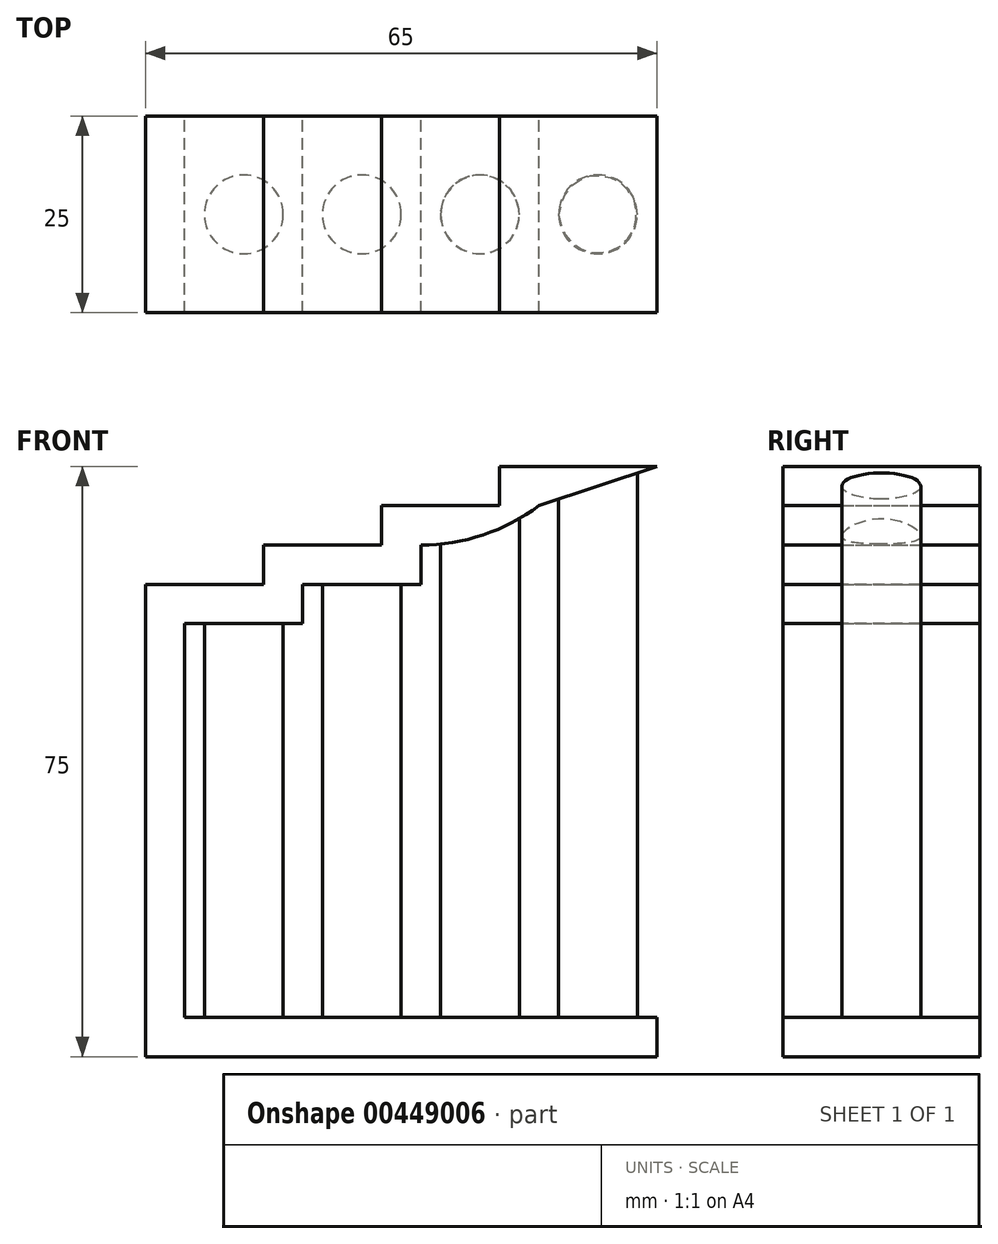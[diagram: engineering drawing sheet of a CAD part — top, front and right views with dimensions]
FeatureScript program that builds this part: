
annotation { "Feature Type Name" : "Feature", "Feature Type Description" : "" }
export const myFeature = defineFeature(function(context is Context, id is Id, definition is map)
    precondition{}
    {
        {
            var Q0;
            Q0=qCreatedBy(makeId("Front.planeOp"),FACE);
            var sketch = newSketch(context, id + "F0", { "sketchPlane" : qUnion([Q0])});
            skLineSegment(sketch, "E0.bottom", {"start": v(0, 0) * mm, "end": v(65, 0) * mm});
            skLineSegment(sketch, "E0.top", {"start": v(0, 5) * mm, "end": v(65, 5) * mm});
            skLineSegment(sketch, "E0.left", {"start": v(0, 0) * mm, "end": v(0, 5) * mm});
            skLineSegment(sketch, "E0.right", {"start": v(65, 0) * mm, "end": v(65, 5) * mm});
            skLineSegment(sketch, "E1.bottom", {"start": v(0, 5) * mm, "end": v(5, 5) * mm});
            skLineSegment(sketch, "E1.top", {"start": v(0, 55) * mm, "end": v(5, 55) * mm});
            skLineSegment(sketch, "E1.left", {"start": v(0, 5) * mm, "end": v(0, 55) * mm});
            skLineSegment(sketch, "E1.right", {"start": v(5, 5) * mm, "end": v(5, 55) * mm});
            skLineSegment(sketch, "E2", {"start": v(0, 55) * mm, "end": v(20, 55) * mm});
            skLineSegment(sketch, "E3", {"start": v(20, 55) * mm, "end": v(20, 60) * mm});
            skLineSegment(sketch, "E4", {"start": v(20, 60) * mm, "end": v(35, 60) * mm});
            skLineSegment(sketch, "E5", {"start": v(35, 60) * mm, "end": v(35, 65) * mm});
            skLineSegment(sketch, "E6", {"start": v(35, 65) * mm, "end": v(50, 65) * mm, "construction": true});
            skLineSegment(sketch, "E7", {"start": v(50, 65) * mm, "end": v(50, 70) * mm, "construction": true});
            skLineSegment(sketch, "E8", {"start": v(50, 70) * mm, "end": v(65, 70) * mm, "construction": true});
            skLineSegment(sketch, "E9", {"start": v(65, 70) * mm, "end": v(65, 75) * mm, "construction": true});
            skLineSegment(sketch, "E10", {"start": v(65, 75) * mm, "end": v(45, 75) * mm});
            skLineSegment(sketch, "E11", {"start": v(45, 75) * mm, "end": v(45, 70) * mm});
            skLineSegment(sketch, "E12", {"start": v(45, 70) * mm, "end": v(30, 70) * mm});
            skLineSegment(sketch, "E13", {"start": v(30, 70) * mm, "end": v(30, 65) * mm});
            skLineSegment(sketch, "E14", {"start": v(30, 65) * mm, "end": v(15, 65) * mm});
            skLineSegment(sketch, "E15", {"start": v(15, 65) * mm, "end": v(15, 60) * mm});
            skLineSegment(sketch, "E16", {"start": v(15, 60) * mm, "end": v(0, 60) * mm});
            skLineSegment(sketch, "E17", {"start": v(0, 60) * mm, "end": v(0, 55) * mm});
            skLineSegment(sketch, "E18", {"start": v(5, 55) * mm, "end": v(20, 55) * mm});
            skLineSegment(sketch, "E19", {"start": v(50, 70) * mm, "end": v(65, 75) * mm});
            skArc(sketch, "E20", {"start": v(35, 65) * mm, "mid": v(42.9, 66.28) * mm, "end": v(50, 70) * mm});
            skSolve(sketch);
        }
        {
            var Q0;
            Q0=qSketchRegion(id+"F0",true);
            extrude(context, id + "F1", {"entities" : qUnion([Q0]), "depth" : 25 * mm});
        }
        {
            var Q0;
            Q0=makeQuery(id+"F1.opExtrude","SWEPT_FACE",FACE,{"disambiguationData":[OSD([sQuery(id+"F0.wireOp",EDGE,"E0.top")])]});
            var sketch = newSketch(context, id + "F2", { "sketchPlane" : qUnion([Q0])});
            skLineSegment(sketch, "E21.0", {"start": v(50, -25) * mm, "end": v(50, 0) * mm, "construction": true});
            skLineSegment(sketch, "E22.0", {"start": v(35, -25) * mm, "end": v(35, 0) * mm, "construction": true});
            skPoint(sketch, "E23.0", {"position": v(20, -12.5) * mm});
            skLineSegment(sketch, "E24.0", {"start": v(20, -25) * mm, "end": v(20, 0) * mm, "construction": true});
            skLineSegment(sketch, "E25", {"start": v(20, -12.5) * mm, "end": v(5, -12.5) * mm, "construction": true});
            skLineSegment(sketch, "E26", {"start": v(20, -12.5) * mm, "end": v(35, -12.5) * mm, "construction": true});
            skLineSegment(sketch, "E27", {"start": v(35, -12.5) * mm, "end": v(50, -12.5) * mm, "construction": true});
            skLineSegment(sketch, "E28", {"start": v(50, -12.5) * mm, "end": v(65, -12.5) * mm, "construction": true});
            skPoint(sketch, "E29", {"position": v(12.5, -12.5) * mm});
            skPoint(sketch, "E30", {"position": v(27.5, -12.5) * mm});
            skPoint(sketch, "E31", {"position": v(42.5, -12.5) * mm});
            skPoint(sketch, "E32", {"position": v(57.5, -12.5) * mm});
            skCircle(sketch, "E33", {"center": v(12.5, -12.5) * mm, "radius": 5 * mm});
            skCircle(sketch, "E34", {"center": v(27.5, -12.5) * mm, "radius": 5 * mm});
            skCircle(sketch, "E35", {"center": v(42.5, -12.5) * mm, "radius": 5 * mm});
            skCircle(sketch, "E36", {"center": v(57.5, -12.5) * mm, "radius": 5 * mm});
            skSolve(sketch);
        }
        {
            var Q0;
            Q0=makeQuery(id+"F2.imprint","IMPRINT",FACE,{"disambiguationData":[TD([[makeQuery(id+"F2.imprint","IMPRINT",EDGE,{"derivedFrom":sQuery(id+"F2.wireOp",EDGE,"E33")}),1.0]])]});
            var Q1;
            Q1=makeQuery(id+"F2.imprint","IMPRINT",FACE,{"disambiguationData":[TD([[makeQuery(id+"F2.imprint","IMPRINT",EDGE,{"derivedFrom":sQuery(id+"F2.wireOp",EDGE,"E34")}),1.0]])]});
            var Q2;
            Q2=makeQuery(id+"F2.imprint","IMPRINT",FACE,{"disambiguationData":[TD([[makeQuery(id+"F2.imprint","IMPRINT",EDGE,{"derivedFrom":sQuery(id+"F2.wireOp",EDGE,"E35")}),1.0]])]});
            var Q3;
            Q3=makeQuery(id+"F2.imprint","IMPRINT",FACE,{"disambiguationData":[TD([[makeQuery(id+"F2.imprint","IMPRINT",EDGE,{"derivedFrom":sQuery(id+"F2.wireOp",EDGE,"E36")}),1.0]])]});
            var Q4;
            Q4=sQuery(id+"F0.wireOp",EDGE,"E7");
            var Q5;
            Q5=sQuery(id+"F0.wireOp",EDGE,"E6");
            var Q6;
            Q6=sQuery(id+"F0.wireOp",EDGE,"E9");
            var Q7;
            Q7=sQuery(id+"F0.wireOp",EDGE,"E8");
            var Q8;
            Q8=sQuery(id+"F2.wireOp",EDGE,"E33");
            var Q9;
            Q9=sQuery(id+"F2.wireOp",EDGE,"E34");
            var Q10;
            Q10=sQuery(id+"F2.wireOp",EDGE,"E35");
            var Q11;
            Q11=sQuery(id+"F2.wireOp",EDGE,"E36");
            extrude(context, id + "F3", {"entities" : qUnion([Q0, Q1, Q2, Q3]), "surfaceEntities" : qUnion([Q4, Q5, Q6, Q7, Q8, Q9, Q10, Q11]), "endBound" : BoundingType.UP_TO_NEXT, "depth" : 25 * mm});
        }
    });
